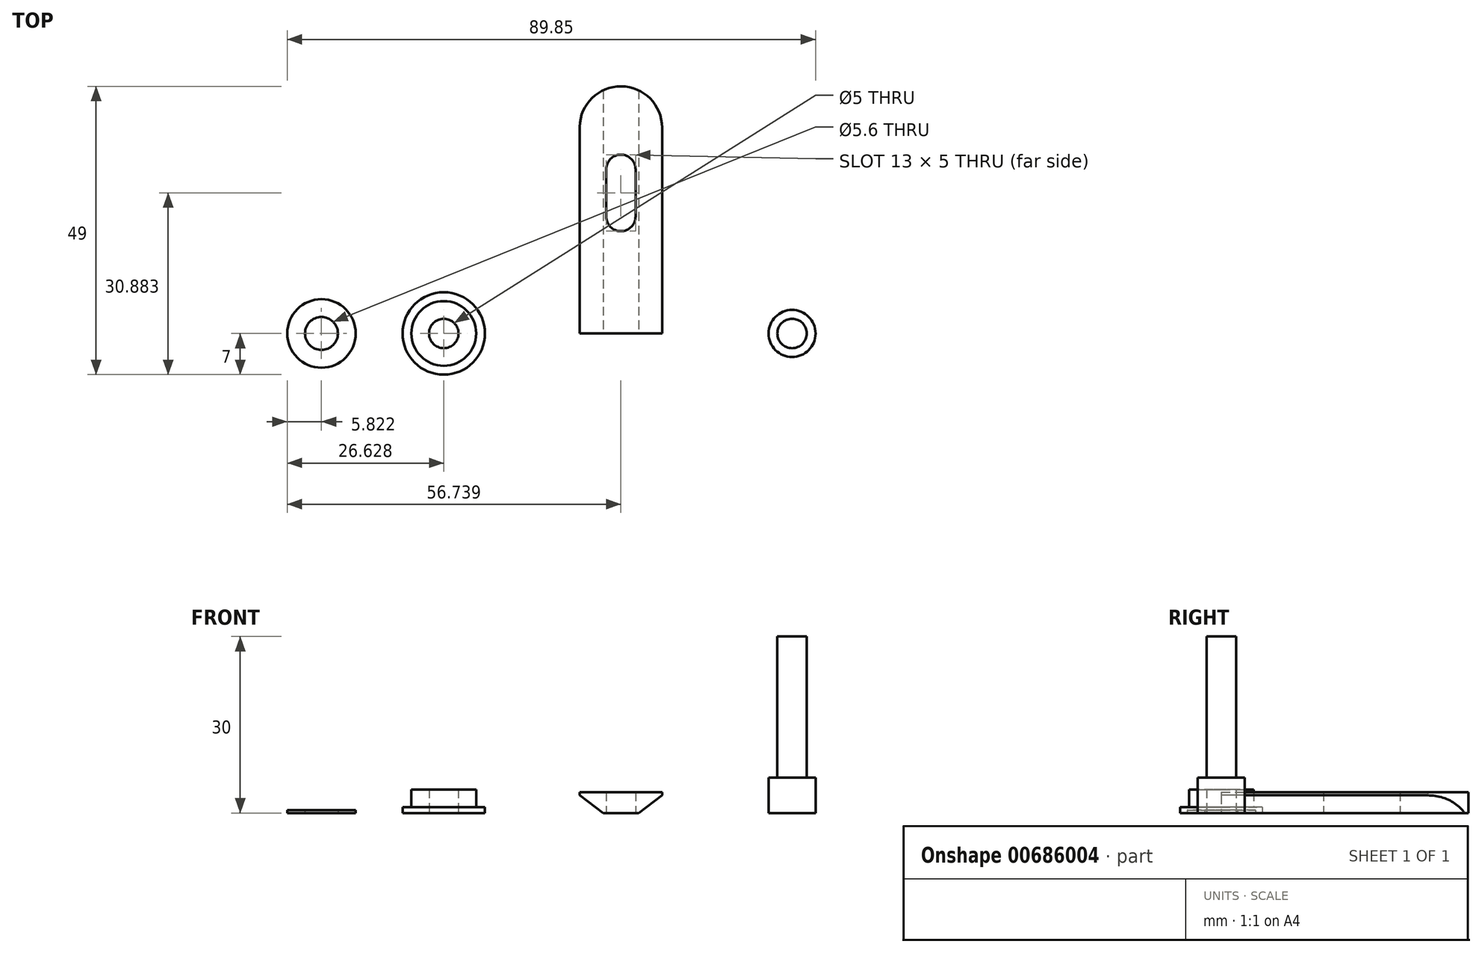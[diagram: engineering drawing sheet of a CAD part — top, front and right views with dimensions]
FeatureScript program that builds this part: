
annotation { "Feature Type Name" : "Feature", "Feature Type Description" : "" }
export const myFeature = defineFeature(function(context is Context, id is Id, definition is map)
    precondition{}
    {
        {
            var Q0;
            Q0=qCreatedBy(makeId("Top.planeOp"),FACE);
            var sketch = newSketch(context, id + "F0", { "sketchPlane" : qUnion([Q0])});
            skCircle(sketch, "E0", {"center": v(-43.12, 0) * mm, "radius": 5.5 * mm});
            skCircle(sketch, "E1", {"center": v(-43.12, 0) * mm, "radius": 7 * mm});
            skLineSegment(sketch, "E2", {"start": v(-20.01, 0) * mm, "end": v(-6.01, 0) * mm});
            skLineSegment(sketch, "E3", {"start": v(-6.01, 0) * mm, "end": v(-6.01, 35) * mm});
            skLineSegment(sketch, "E4", {"start": v(-20.01, 0) * mm, "end": v(-20.01, 35.12) * mm});
            skArc(sketch, "E5", {"start": v(-6.01, 35) * mm, "mid": v(-12.95, 42) * mm, "end": v(-20.01, 35.12) * mm});
            skLineSegment(sketch, "E6", {"start": v(-13.01, 27.88) * mm, "end": v(-13.01, 19.88) * mm, "construction": true});
            skArc(sketch, "E7.0.startCap", {"start": v(-15.51, 27.88) * mm, "mid": v(-13.01, 30.38) * mm, "end": v(-10.51, 27.88) * mm});
            skArc(sketch, "E7.0.endCap", {"start": v(-10.51, 19.88) * mm, "mid": v(-13.01, 17.38) * mm, "end": v(-15.51, 19.88) * mm});
            skLineSegment(sketch, "E7.0.left", {"start": v(-10.51, 27.88) * mm, "end": v(-10.51, 19.88) * mm});
            skLineSegment(sketch, "E7.0.right", {"start": v(-15.51, 27.88) * mm, "end": v(-15.51, 19.88) * mm});
            skLineSegment(sketch, "E8", {"start": v(-13.01, 35) * mm, "end": v(-13.01, 0) * mm, "construction": true});
            skCircle(sketch, "E9", {"center": v(-63.93, 0) * mm, "radius": 5.83 * mm});
            skCircle(sketch, "E10", {"center": v(-63.93, 0) * mm, "radius": 2.8 * mm});
            skCircle(sketch, "E11", {"center": v(-43.12, 0) * mm, "radius": 2.5 * mm});
            skCircle(sketch, "E12", {"center": v(16.1, 0) * mm, "radius": 4 * mm});
            skCircle(sketch, "E13", {"center": v(16.1, 0) * mm, "radius": 2.5 * mm});
            skSolve(sketch);
        }
        {
            var Q0;
            Q0=makeQuery(id+"F0.imprint","IMPRINT",FACE,{"disambiguationData":[TD([[makeQuery(id+"F0.imprint","IMPRINT",EDGE,{"derivedFrom":sQuery(id+"F0.wireOp",EDGE,"E2")}),1.0]])]});
            extrude(context, id + "F1", {"entities" : qUnion([Q0]), "depth" : 3.5 * mm, "offsetDistance" : 25 * mm});
        }
        {
            var Q0;
            Q0=makeQuery(id+"F1.opExtrude","SWEPT_FACE",FACE,{"disambiguationData":[OSD([sQuery(id+"F0.wireOp",EDGE,"E2")])]});
            var sketch = newSketch(context, id + "F2", { "sketchPlane" : qUnion([Q0])});
            skLineSegment(sketch, "E14", {"start": v(-20.01, 3) * mm, "end": v(-16.01, 0) * mm});
            skLineSegment(sketch, "E15", {"start": v(-10.01, 0) * mm, "end": v(-6.01, 3) * mm});
            skSolve(sketch);
        }
        {
            var Q0;
            {var subQ0=sQuery(id+"F2.wireOp",EDGE,"E14");Q0=makeQuery(id+"F2.imprint","IMPRINT",FACE,{"disambiguationData":[TD([[makeQuery(id+"F2.imprint","IMPRINT",EDGE,{"derivedFrom":subQ0}),-1.0]])]});}
            var Q1;
            {var subQ0=sQuery(id+"F2.wireOp",EDGE,"E15");Q1=makeQuery(id+"F2.imprint","IMPRINT",FACE,{"disambiguationData":[TD([[makeQuery(id+"F2.imprint","IMPRINT",EDGE,{"derivedFrom":subQ0}),-1.0]])]});}
            extrude(context, id + "F3", {"entities" : qUnion([Q0, Q1]), "operationType" : NewBodyOperationType.REMOVE, "endBound" : BoundingType.THROUGH_ALL, "oppositeDirection" : true, "depth" : 25 * mm, "offsetDistance" : 25 * mm});
        }
        {
            var Q0;
            Q0=makeQuery(id+"F0.imprint","IMPRINT",FACE,{"disambiguationData":[TD([[makeQuery(id+"F0.imprint","IMPRINT",EDGE,{"derivedFrom":sQuery(id+"F0.wireOp",EDGE,"E0")}),1.0]])]});
            extrude(context, id + "F4", {"entities" : qUnion([Q0]), "depth" : 4 * mm, "offsetDistance" : 25 * mm});
        }
        {
            var Q0;
            Q0=makeQuery(id+"F0.imprint","IMPRINT",FACE,{"disambiguationData":[TD([[makeQuery(id+"F0.imprint","IMPRINT",EDGE,{"derivedFrom":sQuery(id+"F0.wireOp",EDGE,"E0")}),-1.0]])]});
            extrude(context, id + "F5", {"entities" : qUnion([Q0]), "operationType" : NewBodyOperationType.ADD, "depth" : 1 * mm, "offsetDistance" : 25 * mm});
        }
        {
            var Q0;
            Q0=makeQuery(id+"F0.imprint","IMPRINT",FACE,{"disambiguationData":[TD([[makeQuery(id+"F0.imprint","IMPRINT",EDGE,{"derivedFrom":sQuery(id+"F0.wireOp",EDGE,"E9")}),1.0]])]});
            extrude(context, id + "F6", {"entities" : qUnion([Q0]), "depth" : 0.5 * mm, "offsetDistance" : 25 * mm});
        }
        {
            var Q0;
            Q0=makeQuery(id+"F0.imprint","IMPRINT",FACE,{"disambiguationData":[TD([[makeQuery(id+"F0.imprint","IMPRINT",EDGE,{"derivedFrom":sQuery(id+"F0.wireOp",EDGE,"E13")}),1.0]])]});
            var Q1;
            Q1=sQuery(id+"F0.wireOp",EDGE,"E13");
            extrude(context, id + "F7", {"entities" : qUnion([Q0]), "surfaceEntities" : qUnion([Q1]), "depth" : 30 * mm, "offsetDistance" : 25 * mm});
        }
        {
            var Q0;
            Q0=makeQuery(id+"F0.imprint","IMPRINT",FACE,{"disambiguationData":[TD([[makeQuery(id+"F0.imprint","IMPRINT",EDGE,{"derivedFrom":sQuery(id+"F0.wireOp",EDGE,"E12")}),1.0]])]});
            var Q1;
            Q1=sQuery(id+"F0.wireOp",EDGE,"E12");
            extrude(context, id + "F8", {"entities" : qUnion([Q0]), "operationType" : NewBodyOperationType.ADD, "surfaceEntities" : qUnion([Q1]), "depth" : 6 * mm, "offsetDistance" : 25 * mm});
        }
    });
